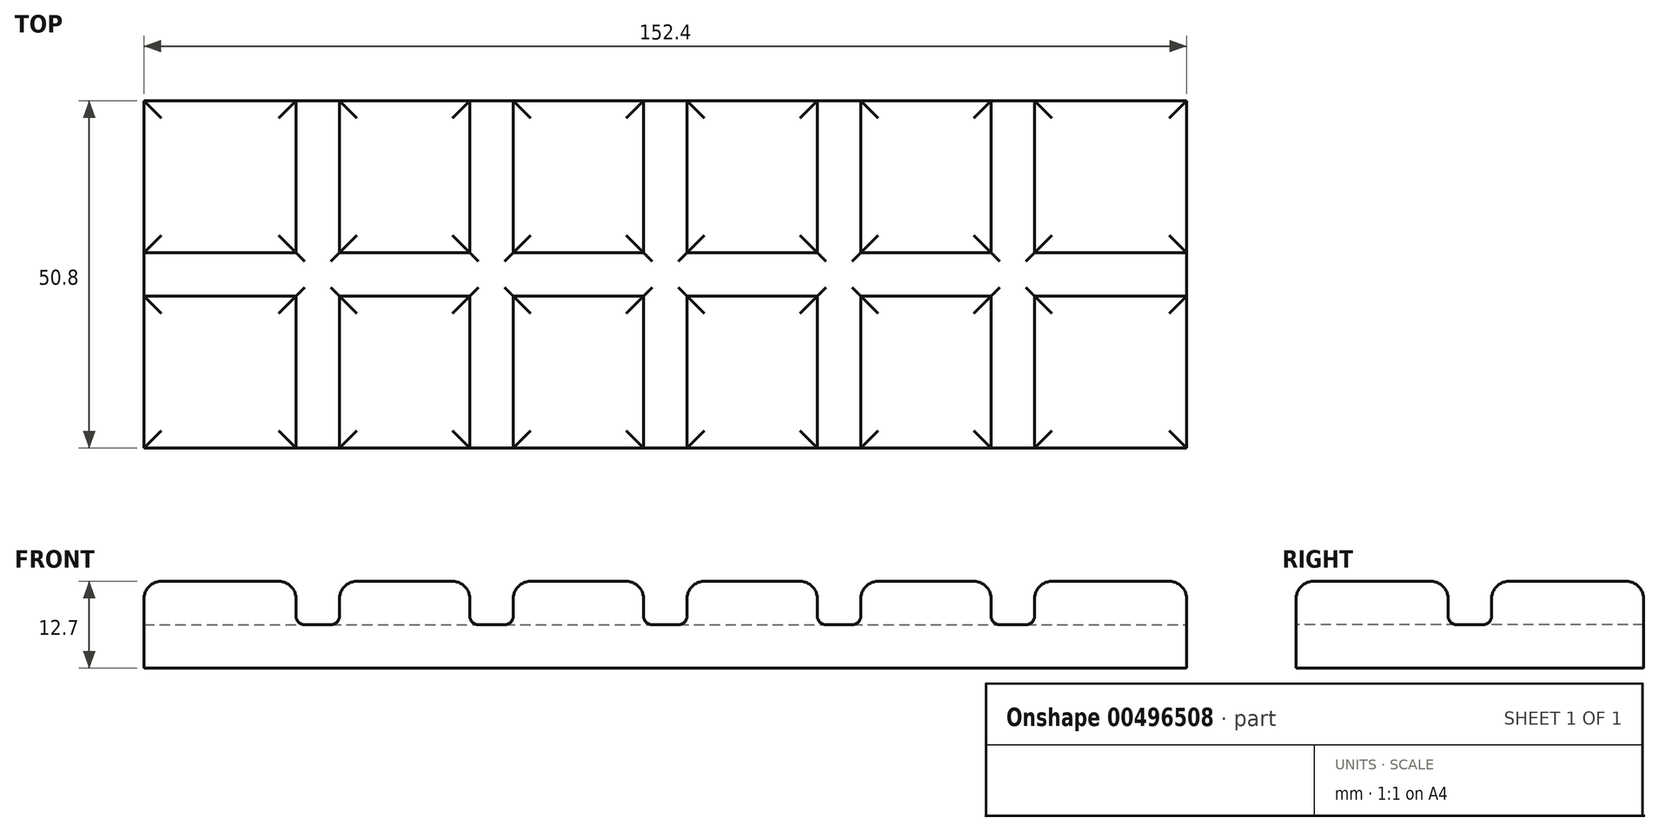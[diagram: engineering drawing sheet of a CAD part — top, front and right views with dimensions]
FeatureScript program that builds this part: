
annotation { "Feature Type Name" : "Feature", "Feature Type Description" : "" }
export const myFeature = defineFeature(function(context is Context, id is Id, definition is map)
    precondition{}
    {
        {
            var Q0;
            Q0=qCreatedBy(makeId("Top.planeOp"),FACE);
            var sketch = newSketch(context, id + "F0", { "sketchPlane" : qUnion([Q0])});
            skLineSegment(sketch, "E0.bottom", {"start": v(-76.2, 25.4) * mm, "end": v(76.2, 25.4) * mm});
            skLineSegment(sketch, "E0.top", {"start": v(-76.2, -25.4) * mm, "end": v(76.2, -25.4) * mm});
            skLineSegment(sketch, "E0.left", {"start": v(-76.2, 25.4) * mm, "end": v(-76.2, -25.4) * mm});
            skLineSegment(sketch, "E0.right", {"start": v(76.2, 25.4) * mm, "end": v(76.2, -25.4) * mm});
            skPoint(sketch, "E0.middle", {"position": v(0, 0) * mm});
            skSolve(sketch);
        }
        {
            var Q0;
            Q0 = qSketchRegion(id + "F0", true);
            extrude(context, id + "F1", {"entities" : qUnion([Q0]), "depth" : 12.7 * mm});
        }
        {
            var Q0;
            Q0=makeQuery(id+"F1.opExtrude","SWEPT_FACE",FACE,{"disambiguationData":[OSD([sQuery(id+"F0.wireOp",EDGE,"E0.right")])]});
            var sketch = newSketch(context, id + "F2", { "sketchPlane" : qUnion([Q0])});
            skLineSegment(sketch, "E1.bottom", {"start": v(3.18, 19.05) * mm, "end": v(-3.17, 19.05) * mm});
            skLineSegment(sketch, "E1.top", {"start": v(3.18, 6.35) * mm, "end": v(-3.17, 6.35) * mm});
            skLineSegment(sketch, "E1.left", {"start": v(3.18, 19.05) * mm, "end": v(3.18, 6.35) * mm});
            skLineSegment(sketch, "E1.right", {"start": v(-3.17, 19.05) * mm, "end": v(-3.17, 6.35) * mm});
            skPoint(sketch, "E1.middle", {"position": v(0, 12.7) * mm});
            skSolve(sketch);
        }
        {
            var Q0;
            Q0 = qSketchRegion(id + "F2", true);
            var Q1;
            Q1=makeQuery(id+"F1.opExtrude","SWEPT_FACE",FACE,{"disambiguationData":[OSD([sQuery(id+"F0.wireOp",EDGE,"E0.left")])]});
            extrude(context, id + "F3", {"entities" : qUnion([Q0]), "operationType" : NewBodyOperationType.REMOVE, "endBound" : BoundingType.THROUGH_ALL, "oppositeDirection" : true, "endBoundEntityFace" : qUnion([Q1]), "depth" : 25.4 * mm});
        }
        {
            var Q0;
            Q0=makeQuery(id+"F1.opExtrude","SWEPT_FACE",FACE,{"disambiguationData":[OSD([sQuery(id+"F0.wireOp",EDGE,"E0.top")])]});
            var sketch = newSketch(context, id + "F4", { "sketchPlane" : qUnion([Q0])});
            skLineSegment(sketch, "E2", {"start": v(-81.97, 6.35) * mm, "end": v(82.24, 6.35) * mm, "construction": true});
            skPoint(sketch, "E2.startSnap0", {"position": v(-76.2, 6.35) * mm});
            skLineSegment(sketch, "E3.bottom", {"start": v(3.18, 6.35) * mm, "end": v(-3.17, 6.35) * mm});
            skLineSegment(sketch, "E3.top", {"start": v(3.18, 19.05) * mm, "end": v(-3.17, 19.05) * mm});
            skLineSegment(sketch, "E3.left", {"start": v(3.18, 6.35) * mm, "end": v(3.18, 19.05) * mm});
            skLineSegment(sketch, "E3.right", {"start": v(-3.17, 6.35) * mm, "end": v(-3.17, 19.05) * mm});
            skPoint(sketch, "E3.middle", {"position": v(0, 12.7) * mm});
            skLineSegment(sketch, "E4.bottom", {"start": v(28.58, 6.35) * mm, "end": v(22.23, 6.35) * mm});
            skLineSegment(sketch, "E4.top", {"start": v(28.58, 19.05) * mm, "end": v(22.23, 19.05) * mm});
            skLineSegment(sketch, "E4.left", {"start": v(28.58, 6.35) * mm, "end": v(28.58, 19.05) * mm});
            skLineSegment(sketch, "E4.right", {"start": v(22.23, 6.35) * mm, "end": v(22.23, 19.05) * mm});
            skPoint(sketch, "E4.middle", {"position": v(25.4, 12.7) * mm});
            skLineSegment(sketch, "E5.bottom", {"start": v(53.98, 6.35) * mm, "end": v(47.63, 6.35) * mm});
            skLineSegment(sketch, "E5.top", {"start": v(53.98, 19.05) * mm, "end": v(47.63, 19.05) * mm});
            skLineSegment(sketch, "E5.left", {"start": v(53.98, 6.35) * mm, "end": v(53.98, 19.05) * mm});
            skLineSegment(sketch, "E5.right", {"start": v(47.63, 6.35) * mm, "end": v(47.63, 19.05) * mm});
            skPoint(sketch, "E5.middle", {"position": v(50.8, 12.7) * mm});
            skLineSegment(sketch, "E6.bottom", {"start": v(-22.23, 6.35) * mm, "end": v(-28.58, 6.35) * mm});
            skLineSegment(sketch, "E6.top", {"start": v(-22.23, 19.05) * mm, "end": v(-28.58, 19.05) * mm});
            skLineSegment(sketch, "E6.left", {"start": v(-22.23, 6.35) * mm, "end": v(-22.23, 19.05) * mm});
            skLineSegment(sketch, "E6.right", {"start": v(-28.58, 6.35) * mm, "end": v(-28.58, 19.05) * mm});
            skPoint(sketch, "E6.middle", {"position": v(-25.4, 12.7) * mm});
            skLineSegment(sketch, "E7.bottom", {"start": v(-47.63, 6.35) * mm, "end": v(-53.98, 6.35) * mm});
            skLineSegment(sketch, "E7.top", {"start": v(-47.63, 19.05) * mm, "end": v(-53.98, 19.05) * mm});
            skLineSegment(sketch, "E7.left", {"start": v(-47.63, 6.35) * mm, "end": v(-47.63, 19.05) * mm});
            skLineSegment(sketch, "E7.right", {"start": v(-53.98, 6.35) * mm, "end": v(-53.98, 19.05) * mm});
            skPoint(sketch, "E7.middle", {"position": v(-50.8, 12.7) * mm});
            skSolve(sketch);
        }
        {
            var Q0;
            Q0 = qSketchRegion(id + "F4", true);
            extrude(context, id + "F5", {"entities" : qUnion([Q0]), "operationType" : NewBodyOperationType.REMOVE, "endBound" : BoundingType.THROUGH_ALL, "oppositeDirection" : true, "depth" : 25.4 * mm});
        }
        {
            var Q0;
            {var subQ0=sQuery(id+"F0.wireOp",EDGE,"E0.top");var subQ1=makeQuery(id+"F1.opExtrude","SWEPT_FACE",FACE,{"disambiguationData":[OSD([subQ0])]});var subQ2=sQuery(id+"F0.wireOp",EDGE,"E0.left");var subQ3=makeQuery(id+"F1.opExtrude","SWEPT_FACE",FACE,{"disambiguationData":[OSD([subQ2])]});var subQ5=sQuery(id+"F0.wireOp",EDGE,"E0.right");Q0=makeQuery(id+"F5.boolean.opBoolean","SPLIT",FACE,{"disambiguationData":[TD([subQ3])],"derivedFrom":makeQuery(id+"F3.boolean.opBoolean","SPLIT",FACE,{"disambiguationData":[TD([subQ1])],"derivedFrom":makeQuery(id+"F1.opExtrude","CAP_FACE",FACE,{"disambiguationData":[OSD([sQuery(id+"F0.wireOp",EDGE,"E0.bottom"),subQ0,subQ2,subQ5])],"isStart":false})})});}
            var Q1;
            {var subQ0=sQuery(id+"F0.wireOp",EDGE,"E0.top");var subQ1=makeQuery(id+"F1.opExtrude","SWEPT_FACE",FACE,{"disambiguationData":[OSD([subQ0])]});var subQ3=sQuery(id+"F0.wireOp",EDGE,"E0.left");var subQ4=sQuery(id+"F0.wireOp",EDGE,"E0.right");Q1=makeQuery(id+"F5.boolean.opBoolean","SPLIT",FACE,{"disambiguationData":[TD([makeQuery(id+"F5.opExtrude","SWEPT_FACE",FACE,{"disambiguationData":[OSD([sQuery(id+"F4.wireOp",EDGE,"E6.right")])]})])],"derivedFrom":makeQuery(id+"F3.boolean.opBoolean","SPLIT",FACE,{"disambiguationData":[TD([subQ1])],"derivedFrom":makeQuery(id+"F1.opExtrude","CAP_FACE",FACE,{"disambiguationData":[OSD([sQuery(id+"F0.wireOp",EDGE,"E0.bottom"),subQ0,subQ3,subQ4])],"isStart":false})})});}
            var Q2;
            {var subQ0=sQuery(id+"F0.wireOp",EDGE,"E0.top");var subQ1=makeQuery(id+"F1.opExtrude","SWEPT_FACE",FACE,{"disambiguationData":[OSD([subQ0])]});var subQ3=sQuery(id+"F0.wireOp",EDGE,"E0.left");var subQ4=sQuery(id+"F0.wireOp",EDGE,"E0.right");Q2=makeQuery(id+"F5.boolean.opBoolean","SPLIT",FACE,{"disambiguationData":[TD([makeQuery(id+"F5.opExtrude","SWEPT_FACE",FACE,{"disambiguationData":[OSD([sQuery(id+"F4.wireOp",EDGE,"E3.right")])]})])],"derivedFrom":makeQuery(id+"F3.boolean.opBoolean","SPLIT",FACE,{"disambiguationData":[TD([subQ1])],"derivedFrom":makeQuery(id+"F1.opExtrude","CAP_FACE",FACE,{"disambiguationData":[OSD([sQuery(id+"F0.wireOp",EDGE,"E0.bottom"),subQ0,subQ3,subQ4])],"isStart":false})})});}
            var Q3;
            {var subQ0=sQuery(id+"F0.wireOp",EDGE,"E0.top");var subQ1=makeQuery(id+"F1.opExtrude","SWEPT_FACE",FACE,{"disambiguationData":[OSD([subQ0])]});var subQ3=sQuery(id+"F0.wireOp",EDGE,"E0.left");var subQ4=sQuery(id+"F0.wireOp",EDGE,"E0.right");Q3=makeQuery(id+"F5.boolean.opBoolean","SPLIT",FACE,{"disambiguationData":[TD([makeQuery(id+"F5.opExtrude","SWEPT_FACE",FACE,{"disambiguationData":[OSD([sQuery(id+"F4.wireOp",EDGE,"E3.left")])]})])],"derivedFrom":makeQuery(id+"F3.boolean.opBoolean","SPLIT",FACE,{"disambiguationData":[TD([subQ1])],"derivedFrom":makeQuery(id+"F1.opExtrude","CAP_FACE",FACE,{"disambiguationData":[OSD([sQuery(id+"F0.wireOp",EDGE,"E0.bottom"),subQ0,subQ3,subQ4])],"isStart":false})})});}
            var Q4;
            {var subQ0=sQuery(id+"F0.wireOp",EDGE,"E0.top");var subQ1=makeQuery(id+"F1.opExtrude","SWEPT_FACE",FACE,{"disambiguationData":[OSD([subQ0])]});var subQ3=sQuery(id+"F0.wireOp",EDGE,"E0.left");var subQ4=sQuery(id+"F0.wireOp",EDGE,"E0.right");Q4=makeQuery(id+"F5.boolean.opBoolean","SPLIT",FACE,{"disambiguationData":[TD([makeQuery(id+"F5.opExtrude","SWEPT_FACE",FACE,{"disambiguationData":[OSD([sQuery(id+"F4.wireOp",EDGE,"E4.left")])]})])],"derivedFrom":makeQuery(id+"F3.boolean.opBoolean","SPLIT",FACE,{"disambiguationData":[TD([subQ1])],"derivedFrom":makeQuery(id+"F1.opExtrude","CAP_FACE",FACE,{"disambiguationData":[OSD([sQuery(id+"F0.wireOp",EDGE,"E0.bottom"),subQ0,subQ3,subQ4])],"isStart":false})})});}
            var Q5;
            {var subQ0=sQuery(id+"F0.wireOp",EDGE,"E0.top");var subQ1=makeQuery(id+"F1.opExtrude","SWEPT_FACE",FACE,{"disambiguationData":[OSD([subQ0])]});var subQ2=sQuery(id+"F0.wireOp",EDGE,"E0.right");var subQ3=makeQuery(id+"F1.opExtrude","SWEPT_FACE",FACE,{"disambiguationData":[OSD([subQ2])]});var subQ5=sQuery(id+"F0.wireOp",EDGE,"E0.left");Q5=makeQuery(id+"F5.boolean.opBoolean","SPLIT",FACE,{"disambiguationData":[TD([subQ3])],"derivedFrom":makeQuery(id+"F3.boolean.opBoolean","SPLIT",FACE,{"disambiguationData":[TD([subQ1])],"derivedFrom":makeQuery(id+"F1.opExtrude","CAP_FACE",FACE,{"disambiguationData":[OSD([sQuery(id+"F0.wireOp",EDGE,"E0.bottom"),subQ0,subQ5,subQ2])],"isStart":false})})});}
            var Q6;
            {var subQ0=sQuery(id+"F0.wireOp",EDGE,"E0.bottom");var subQ1=makeQuery(id+"F1.opExtrude","SWEPT_FACE",FACE,{"disambiguationData":[OSD([subQ0])]});var subQ2=sQuery(id+"F0.wireOp",EDGE,"E0.right");var subQ3=makeQuery(id+"F1.opExtrude","SWEPT_FACE",FACE,{"disambiguationData":[OSD([subQ2])]});var subQ5=sQuery(id+"F0.wireOp",EDGE,"E0.left");Q6=makeQuery(id+"F5.boolean.opBoolean","SPLIT",FACE,{"disambiguationData":[TD([subQ3])],"derivedFrom":makeQuery(id+"F3.boolean.opBoolean","SPLIT",FACE,{"disambiguationData":[TD([subQ1])],"derivedFrom":makeQuery(id+"F1.opExtrude","CAP_FACE",FACE,{"disambiguationData":[OSD([subQ0,sQuery(id+"F0.wireOp",EDGE,"E0.top"),subQ5,subQ2])],"isStart":false})})});}
            var Q7;
            {var subQ0=sQuery(id+"F0.wireOp",EDGE,"E0.bottom");var subQ1=makeQuery(id+"F1.opExtrude","SWEPT_FACE",FACE,{"disambiguationData":[OSD([subQ0])]});var subQ3=sQuery(id+"F0.wireOp",EDGE,"E0.right");var subQ4=sQuery(id+"F0.wireOp",EDGE,"E0.left");Q7=makeQuery(id+"F5.boolean.opBoolean","SPLIT",FACE,{"disambiguationData":[TD([makeQuery(id+"F5.opExtrude","SWEPT_FACE",FACE,{"disambiguationData":[OSD([sQuery(id+"F4.wireOp",EDGE,"E4.left")])]})])],"derivedFrom":makeQuery(id+"F3.boolean.opBoolean","SPLIT",FACE,{"disambiguationData":[TD([subQ1])],"derivedFrom":makeQuery(id+"F1.opExtrude","CAP_FACE",FACE,{"disambiguationData":[OSD([subQ0,sQuery(id+"F0.wireOp",EDGE,"E0.top"),subQ4,subQ3])],"isStart":false})})});}
            var Q8;
            {var subQ0=sQuery(id+"F0.wireOp",EDGE,"E0.bottom");var subQ1=makeQuery(id+"F1.opExtrude","SWEPT_FACE",FACE,{"disambiguationData":[OSD([subQ0])]});var subQ3=sQuery(id+"F0.wireOp",EDGE,"E0.right");var subQ4=sQuery(id+"F0.wireOp",EDGE,"E0.left");Q8=makeQuery(id+"F5.boolean.opBoolean","SPLIT",FACE,{"disambiguationData":[TD([makeQuery(id+"F5.opExtrude","SWEPT_FACE",FACE,{"disambiguationData":[OSD([sQuery(id+"F4.wireOp",EDGE,"E3.left")])]})])],"derivedFrom":makeQuery(id+"F3.boolean.opBoolean","SPLIT",FACE,{"disambiguationData":[TD([subQ1])],"derivedFrom":makeQuery(id+"F1.opExtrude","CAP_FACE",FACE,{"disambiguationData":[OSD([subQ0,sQuery(id+"F0.wireOp",EDGE,"E0.top"),subQ4,subQ3])],"isStart":false})})});}
            var Q9;
            {var subQ0=sQuery(id+"F0.wireOp",EDGE,"E0.bottom");var subQ1=makeQuery(id+"F1.opExtrude","SWEPT_FACE",FACE,{"disambiguationData":[OSD([subQ0])]});var subQ3=sQuery(id+"F0.wireOp",EDGE,"E0.right");var subQ4=sQuery(id+"F0.wireOp",EDGE,"E0.left");Q9=makeQuery(id+"F5.boolean.opBoolean","SPLIT",FACE,{"disambiguationData":[TD([makeQuery(id+"F5.opExtrude","SWEPT_FACE",FACE,{"disambiguationData":[OSD([sQuery(id+"F4.wireOp",EDGE,"E6.right")])]})])],"derivedFrom":makeQuery(id+"F3.boolean.opBoolean","SPLIT",FACE,{"disambiguationData":[TD([subQ1])],"derivedFrom":makeQuery(id+"F1.opExtrude","CAP_FACE",FACE,{"disambiguationData":[OSD([subQ0,sQuery(id+"F0.wireOp",EDGE,"E0.top"),subQ4,subQ3])],"isStart":false})})});}
            var Q10;
            {var subQ0=sQuery(id+"F0.wireOp",EDGE,"E0.bottom");var subQ1=makeQuery(id+"F1.opExtrude","SWEPT_FACE",FACE,{"disambiguationData":[OSD([subQ0])]});var subQ3=sQuery(id+"F0.wireOp",EDGE,"E0.right");var subQ4=sQuery(id+"F0.wireOp",EDGE,"E0.left");Q10=makeQuery(id+"F5.boolean.opBoolean","SPLIT",FACE,{"disambiguationData":[TD([makeQuery(id+"F5.opExtrude","SWEPT_FACE",FACE,{"disambiguationData":[OSD([sQuery(id+"F4.wireOp",EDGE,"E3.right")])]})])],"derivedFrom":makeQuery(id+"F3.boolean.opBoolean","SPLIT",FACE,{"disambiguationData":[TD([subQ1])],"derivedFrom":makeQuery(id+"F1.opExtrude","CAP_FACE",FACE,{"disambiguationData":[OSD([subQ0,sQuery(id+"F0.wireOp",EDGE,"E0.top"),subQ4,subQ3])],"isStart":false})})});}
            var Q11;
            {var subQ0=sQuery(id+"F0.wireOp",EDGE,"E0.bottom");var subQ1=makeQuery(id+"F1.opExtrude","SWEPT_FACE",FACE,{"disambiguationData":[OSD([subQ0])]});var subQ3=sQuery(id+"F0.wireOp",EDGE,"E0.left");var subQ4=makeQuery(id+"F1.opExtrude","SWEPT_FACE",FACE,{"disambiguationData":[OSD([subQ3])]});var subQ5=sQuery(id+"F0.wireOp",EDGE,"E0.right");Q11=makeQuery(id+"F5.boolean.opBoolean","SPLIT",FACE,{"disambiguationData":[TD([subQ4])],"derivedFrom":makeQuery(id+"F3.boolean.opBoolean","SPLIT",FACE,{"disambiguationData":[TD([subQ1])],"derivedFrom":makeQuery(id+"F1.opExtrude","CAP_FACE",FACE,{"disambiguationData":[OSD([subQ0,sQuery(id+"F0.wireOp",EDGE,"E0.top"),subQ3,subQ5])],"isStart":false})})});}
            fillet(context, id + "F6", {"entities" : qUnion([Q0, Q1, Q2, Q3, Q4, Q5, Q6, Q7, Q8, Q9, Q10, Q11]), "radius" : 2.54 * mm, "tangentPropagation" : true, "allowEdgeOverflow" : false});
        }
        {
            var Q0;
            {var subQ0=sQuery(id+"F4.wireOp",EDGE,"E7.left");var subQ1=sQuery(id+"F4.wireOp",EDGE,"E7.bottom");Q0=makeQuery(id+"F5.boolean.opBoolean","COPY",EDGE,{"disambiguationData":[TD([makeQuery(id+"F1.opExtrude","SWEPT_FACE",FACE,{"disambiguationData":[OSD([sQuery(id+"F0.wireOp",EDGE,"E0.bottom")])]})])],"derivedFrom":makeQuery(id+"F5.opExtrude","SWEPT_EDGE",EDGE,{"disambiguationData":[OSD([subQ1,subQ0])]})});}
            var Q1;
            {var subQ0=sQuery(id+"F4.wireOp",EDGE,"E7.right");var subQ1=sQuery(id+"F4.wireOp",EDGE,"E7.bottom");Q1=makeQuery(id+"F5.boolean.opBoolean","COPY",EDGE,{"disambiguationData":[TD([makeQuery(id+"F1.opExtrude","SWEPT_FACE",FACE,{"disambiguationData":[OSD([sQuery(id+"F0.wireOp",EDGE,"E0.bottom")])]})])],"derivedFrom":makeQuery(id+"F5.opExtrude","SWEPT_EDGE",EDGE,{"disambiguationData":[OSD([subQ1,subQ0])]})});}
            var Q2;
            {var subQ0=sQuery(id+"F4.wireOp",EDGE,"E7.right");var subQ1=sQuery(id+"F4.wireOp",EDGE,"E7.bottom");Q2=makeQuery(id+"F5.boolean.opBoolean","COPY",EDGE,{"disambiguationData":[TD([makeQuery(id+"F1.opExtrude","SWEPT_FACE",FACE,{"disambiguationData":[OSD([sQuery(id+"F0.wireOp",EDGE,"E0.top")])]})])],"derivedFrom":makeQuery(id+"F5.opExtrude","SWEPT_EDGE",EDGE,{"disambiguationData":[OSD([subQ1,subQ0])]})});}
            var Q3;
            {var subQ0=sQuery(id+"F4.wireOp",EDGE,"E7.left");var subQ1=sQuery(id+"F4.wireOp",EDGE,"E7.bottom");Q3=makeQuery(id+"F5.boolean.opBoolean","COPY",EDGE,{"disambiguationData":[TD([makeQuery(id+"F1.opExtrude","SWEPT_FACE",FACE,{"disambiguationData":[OSD([sQuery(id+"F0.wireOp",EDGE,"E0.top")])]})])],"derivedFrom":makeQuery(id+"F5.opExtrude","SWEPT_EDGE",EDGE,{"disambiguationData":[OSD([subQ1,subQ0])]})});}
            var Q4;
            {var subQ0=sQuery(id+"F4.wireOp",EDGE,"E6.left");var subQ1=sQuery(id+"F4.wireOp",EDGE,"E6.bottom");Q4=makeQuery(id+"F5.boolean.opBoolean","COPY",EDGE,{"disambiguationData":[TD([makeQuery(id+"F1.opExtrude","SWEPT_FACE",FACE,{"disambiguationData":[OSD([sQuery(id+"F0.wireOp",EDGE,"E0.top")])]})])],"derivedFrom":makeQuery(id+"F5.opExtrude","SWEPT_EDGE",EDGE,{"disambiguationData":[OSD([subQ1,subQ0])]})});}
            var Q5;
            {var subQ0=sQuery(id+"F4.wireOp",EDGE,"E6.right");var subQ1=sQuery(id+"F4.wireOp",EDGE,"E6.bottom");Q5=makeQuery(id+"F5.boolean.opBoolean","COPY",EDGE,{"disambiguationData":[TD([makeQuery(id+"F1.opExtrude","SWEPT_FACE",FACE,{"disambiguationData":[OSD([sQuery(id+"F0.wireOp",EDGE,"E0.top")])]})])],"derivedFrom":makeQuery(id+"F5.opExtrude","SWEPT_EDGE",EDGE,{"disambiguationData":[OSD([subQ1,subQ0])]})});}
            var Q6;
            {var subQ0=sQuery(id+"F4.wireOp",EDGE,"E6.right");var subQ1=sQuery(id+"F4.wireOp",EDGE,"E6.bottom");Q6=makeQuery(id+"F5.boolean.opBoolean","COPY",EDGE,{"disambiguationData":[TD([makeQuery(id+"F1.opExtrude","SWEPT_FACE",FACE,{"disambiguationData":[OSD([sQuery(id+"F0.wireOp",EDGE,"E0.bottom")])]})])],"derivedFrom":makeQuery(id+"F5.opExtrude","SWEPT_EDGE",EDGE,{"disambiguationData":[OSD([subQ1,subQ0])]})});}
            var Q7;
            {var subQ0=sQuery(id+"F4.wireOp",EDGE,"E6.left");var subQ1=sQuery(id+"F4.wireOp",EDGE,"E6.bottom");Q7=makeQuery(id+"F5.boolean.opBoolean","COPY",EDGE,{"disambiguationData":[TD([makeQuery(id+"F1.opExtrude","SWEPT_FACE",FACE,{"disambiguationData":[OSD([sQuery(id+"F0.wireOp",EDGE,"E0.bottom")])]})])],"derivedFrom":makeQuery(id+"F5.opExtrude","SWEPT_EDGE",EDGE,{"disambiguationData":[OSD([subQ1,subQ0])]})});}
            var Q8;
            {var subQ0=sQuery(id+"F4.wireOp",EDGE,"E3.bottom");var subQ1=sQuery(id+"F4.wireOp",EDGE,"E3.left");Q8=makeQuery(id+"F5.boolean.opBoolean","COPY",EDGE,{"disambiguationData":[TD([makeQuery(id+"F1.opExtrude","SWEPT_FACE",FACE,{"disambiguationData":[OSD([sQuery(id+"F0.wireOp",EDGE,"E0.top")])]})])],"derivedFrom":makeQuery(id+"F5.opExtrude","SWEPT_EDGE",EDGE,{"disambiguationData":[OSD([subQ0,subQ1])]})});}
            var Q9;
            {var subQ0=sQuery(id+"F4.wireOp",EDGE,"E3.bottom");var subQ1=sQuery(id+"F4.wireOp",EDGE,"E3.left");Q9=makeQuery(id+"F5.boolean.opBoolean","COPY",EDGE,{"disambiguationData":[TD([makeQuery(id+"F1.opExtrude","SWEPT_FACE",FACE,{"disambiguationData":[OSD([sQuery(id+"F0.wireOp",EDGE,"E0.bottom")])]})])],"derivedFrom":makeQuery(id+"F5.opExtrude","SWEPT_EDGE",EDGE,{"disambiguationData":[OSD([subQ0,subQ1])]})});}
            var Q10;
            {var subQ0=sQuery(id+"F4.wireOp",EDGE,"E3.bottom");var subQ1=sQuery(id+"F4.wireOp",EDGE,"E3.right");Q10=makeQuery(id+"F5.boolean.opBoolean","COPY",EDGE,{"disambiguationData":[TD([makeQuery(id+"F1.opExtrude","SWEPT_FACE",FACE,{"disambiguationData":[OSD([sQuery(id+"F0.wireOp",EDGE,"E0.bottom")])]})])],"derivedFrom":makeQuery(id+"F5.opExtrude","SWEPT_EDGE",EDGE,{"disambiguationData":[OSD([subQ0,subQ1])]})});}
            var Q11;
            {var subQ0=sQuery(id+"F4.wireOp",EDGE,"E3.bottom");var subQ1=sQuery(id+"F4.wireOp",EDGE,"E3.right");Q11=makeQuery(id+"F5.boolean.opBoolean","COPY",EDGE,{"disambiguationData":[TD([makeQuery(id+"F1.opExtrude","SWEPT_FACE",FACE,{"disambiguationData":[OSD([sQuery(id+"F0.wireOp",EDGE,"E0.top")])]})])],"derivedFrom":makeQuery(id+"F5.opExtrude","SWEPT_EDGE",EDGE,{"disambiguationData":[OSD([subQ0,subQ1])]})});}
            var Q12;
            {var subQ0=sQuery(id+"F4.wireOp",EDGE,"E4.right");var subQ1=sQuery(id+"F4.wireOp",EDGE,"E4.bottom");Q12=makeQuery(id+"F5.boolean.opBoolean","COPY",EDGE,{"disambiguationData":[TD([makeQuery(id+"F1.opExtrude","SWEPT_FACE",FACE,{"disambiguationData":[OSD([sQuery(id+"F0.wireOp",EDGE,"E0.bottom")])]})])],"derivedFrom":makeQuery(id+"F5.opExtrude","SWEPT_EDGE",EDGE,{"disambiguationData":[OSD([subQ1,subQ0])]})});}
            var Q13;
            {var subQ0=sQuery(id+"F4.wireOp",EDGE,"E4.right");var subQ1=sQuery(id+"F4.wireOp",EDGE,"E4.bottom");Q13=makeQuery(id+"F5.boolean.opBoolean","COPY",EDGE,{"disambiguationData":[TD([makeQuery(id+"F1.opExtrude","SWEPT_FACE",FACE,{"disambiguationData":[OSD([sQuery(id+"F0.wireOp",EDGE,"E0.top")])]})])],"derivedFrom":makeQuery(id+"F5.opExtrude","SWEPT_EDGE",EDGE,{"disambiguationData":[OSD([subQ1,subQ0])]})});}
            var Q14;
            {var subQ0=sQuery(id+"F4.wireOp",EDGE,"E4.left");var subQ1=sQuery(id+"F4.wireOp",EDGE,"E4.bottom");Q14=makeQuery(id+"F5.boolean.opBoolean","COPY",EDGE,{"disambiguationData":[TD([makeQuery(id+"F1.opExtrude","SWEPT_FACE",FACE,{"disambiguationData":[OSD([sQuery(id+"F0.wireOp",EDGE,"E0.top")])]})])],"derivedFrom":makeQuery(id+"F5.opExtrude","SWEPT_EDGE",EDGE,{"disambiguationData":[OSD([subQ1,subQ0])]})});}
            var Q15;
            {var subQ0=sQuery(id+"F4.wireOp",EDGE,"E4.left");var subQ1=sQuery(id+"F4.wireOp",EDGE,"E4.bottom");Q15=makeQuery(id+"F5.boolean.opBoolean","COPY",EDGE,{"disambiguationData":[TD([makeQuery(id+"F1.opExtrude","SWEPT_FACE",FACE,{"disambiguationData":[OSD([sQuery(id+"F0.wireOp",EDGE,"E0.bottom")])]})])],"derivedFrom":makeQuery(id+"F5.opExtrude","SWEPT_EDGE",EDGE,{"disambiguationData":[OSD([subQ1,subQ0])]})});}
            var Q16;
            {var subQ0=sQuery(id+"F4.wireOp",EDGE,"E5.right");var subQ1=sQuery(id+"F4.wireOp",EDGE,"E5.bottom");Q16=makeQuery(id+"F5.boolean.opBoolean","COPY",EDGE,{"disambiguationData":[TD([makeQuery(id+"F1.opExtrude","SWEPT_FACE",FACE,{"disambiguationData":[OSD([sQuery(id+"F0.wireOp",EDGE,"E0.bottom")])]})])],"derivedFrom":makeQuery(id+"F5.opExtrude","SWEPT_EDGE",EDGE,{"disambiguationData":[OSD([subQ1,subQ0])]})});}
            var Q17;
            {var subQ0=sQuery(id+"F4.wireOp",EDGE,"E5.bottom");var subQ1=sQuery(id+"F4.wireOp",EDGE,"E5.right");Q17=makeQuery(id+"F5.boolean.opBoolean","COPY",EDGE,{"disambiguationData":[TD([makeQuery(id+"F1.opExtrude","SWEPT_FACE",FACE,{"disambiguationData":[OSD([sQuery(id+"F0.wireOp",EDGE,"E0.top")])]})])],"derivedFrom":makeQuery(id+"F5.opExtrude","SWEPT_EDGE",EDGE,{"disambiguationData":[OSD([subQ0,subQ1])]})});}
            var Q18;
            {var subQ0=sQuery(id+"F4.wireOp",EDGE,"E5.left");var subQ1=sQuery(id+"F4.wireOp",EDGE,"E5.bottom");Q18=makeQuery(id+"F5.boolean.opBoolean","COPY",EDGE,{"disambiguationData":[TD([makeQuery(id+"F1.opExtrude","SWEPT_FACE",FACE,{"disambiguationData":[OSD([sQuery(id+"F0.wireOp",EDGE,"E0.bottom")])]})])],"derivedFrom":makeQuery(id+"F5.opExtrude","SWEPT_EDGE",EDGE,{"disambiguationData":[OSD([subQ1,subQ0])]})});}
            var Q19;
            {var subQ0=sQuery(id+"F4.wireOp",EDGE,"E5.bottom");var subQ1=sQuery(id+"F4.wireOp",EDGE,"E5.left");Q19=makeQuery(id+"F5.boolean.opBoolean","COPY",EDGE,{"disambiguationData":[TD([makeQuery(id+"F1.opExtrude","SWEPT_FACE",FACE,{"disambiguationData":[OSD([sQuery(id+"F0.wireOp",EDGE,"E0.top")])]})])],"derivedFrom":makeQuery(id+"F5.opExtrude","SWEPT_EDGE",EDGE,{"disambiguationData":[OSD([subQ0,subQ1])]})});}
            var Q20;
            {var subQ0=sQuery(id+"F2.wireOp",EDGE,"E1.right");var subQ1=sQuery(id+"F2.wireOp",EDGE,"E1.top");Q20=makeQuery(id+"F5.boolean.opBoolean","SPLIT",EDGE,{"disambiguationData":[TD([makeQuery(id+"F1.opExtrude","SWEPT_FACE",FACE,{"disambiguationData":[OSD([sQuery(id+"F0.wireOp",EDGE,"E0.right")])]})])],"derivedFrom":makeQuery(id+"F3.boolean.opBoolean","COPY",EDGE,{"derivedFrom":makeQuery(id+"F3.opExtrude","SWEPT_EDGE",EDGE,{"disambiguationData":[OSD([subQ1,subQ0])]})})});}
            var Q21;
            {var subQ0=sQuery(id+"F2.wireOp",EDGE,"E1.right");var subQ1=sQuery(id+"F2.wireOp",EDGE,"E1.top");Q21=makeQuery(id+"F5.boolean.opBoolean","SPLIT",EDGE,{"disambiguationData":[TD([makeQuery(id+"F5.opExtrude","SWEPT_FACE",FACE,{"disambiguationData":[OSD([sQuery(id+"F4.wireOp",EDGE,"E4.left")])]})])],"derivedFrom":makeQuery(id+"F3.boolean.opBoolean","COPY",EDGE,{"derivedFrom":makeQuery(id+"F3.opExtrude","SWEPT_EDGE",EDGE,{"disambiguationData":[OSD([subQ1,subQ0])]})})});}
            var Q22;
            {var subQ0=sQuery(id+"F2.wireOp",EDGE,"E1.right");var subQ1=sQuery(id+"F2.wireOp",EDGE,"E1.top");Q22=makeQuery(id+"F5.boolean.opBoolean","SPLIT",EDGE,{"disambiguationData":[TD([makeQuery(id+"F5.opExtrude","SWEPT_FACE",FACE,{"disambiguationData":[OSD([sQuery(id+"F4.wireOp",EDGE,"E3.left")])]})])],"derivedFrom":makeQuery(id+"F3.boolean.opBoolean","COPY",EDGE,{"derivedFrom":makeQuery(id+"F3.opExtrude","SWEPT_EDGE",EDGE,{"disambiguationData":[OSD([subQ1,subQ0])]})})});}
            var Q23;
            {var subQ0=sQuery(id+"F2.wireOp",EDGE,"E1.right");var subQ1=sQuery(id+"F2.wireOp",EDGE,"E1.top");Q23=makeQuery(id+"F5.boolean.opBoolean","SPLIT",EDGE,{"disambiguationData":[TD([makeQuery(id+"F5.opExtrude","SWEPT_FACE",FACE,{"disambiguationData":[OSD([sQuery(id+"F4.wireOp",EDGE,"E3.right")])]})])],"derivedFrom":makeQuery(id+"F3.boolean.opBoolean","COPY",EDGE,{"derivedFrom":makeQuery(id+"F3.opExtrude","SWEPT_EDGE",EDGE,{"disambiguationData":[OSD([subQ1,subQ0])]})})});}
            var Q24;
            {var subQ0=sQuery(id+"F2.wireOp",EDGE,"E1.right");var subQ1=sQuery(id+"F2.wireOp",EDGE,"E1.top");Q24=makeQuery(id+"F5.boolean.opBoolean","SPLIT",EDGE,{"disambiguationData":[TD([makeQuery(id+"F5.opExtrude","SWEPT_FACE",FACE,{"disambiguationData":[OSD([sQuery(id+"F4.wireOp",EDGE,"E6.right")])]})])],"derivedFrom":makeQuery(id+"F3.boolean.opBoolean","COPY",EDGE,{"derivedFrom":makeQuery(id+"F3.opExtrude","SWEPT_EDGE",EDGE,{"disambiguationData":[OSD([subQ1,subQ0])]})})});}
            var Q25;
            {var subQ0=sQuery(id+"F2.wireOp",EDGE,"E1.right");var subQ1=sQuery(id+"F2.wireOp",EDGE,"E1.top");Q25=makeQuery(id+"F5.boolean.opBoolean","SPLIT",EDGE,{"disambiguationData":[TD([makeQuery(id+"F1.opExtrude","SWEPT_FACE",FACE,{"disambiguationData":[OSD([sQuery(id+"F0.wireOp",EDGE,"E0.left")])]})])],"derivedFrom":makeQuery(id+"F3.boolean.opBoolean","COPY",EDGE,{"derivedFrom":makeQuery(id+"F3.opExtrude","SWEPT_EDGE",EDGE,{"disambiguationData":[OSD([subQ1,subQ0])]})})});}
            var Q26;
            {var subQ0=sQuery(id+"F2.wireOp",EDGE,"E1.left");var subQ1=sQuery(id+"F2.wireOp",EDGE,"E1.top");Q26=makeQuery(id+"F5.boolean.opBoolean","SPLIT",EDGE,{"disambiguationData":[TD([makeQuery(id+"F1.opExtrude","SWEPT_FACE",FACE,{"disambiguationData":[OSD([sQuery(id+"F0.wireOp",EDGE,"E0.left")])]})])],"derivedFrom":makeQuery(id+"F3.boolean.opBoolean","COPY",EDGE,{"derivedFrom":makeQuery(id+"F3.opExtrude","SWEPT_EDGE",EDGE,{"disambiguationData":[OSD([subQ1,subQ0])]})})});}
            var Q27;
            {var subQ0=sQuery(id+"F2.wireOp",EDGE,"E1.left");var subQ1=sQuery(id+"F2.wireOp",EDGE,"E1.top");Q27=makeQuery(id+"F5.boolean.opBoolean","SPLIT",EDGE,{"disambiguationData":[TD([makeQuery(id+"F5.opExtrude","SWEPT_FACE",FACE,{"disambiguationData":[OSD([sQuery(id+"F4.wireOp",EDGE,"E3.right")])]})])],"derivedFrom":makeQuery(id+"F3.boolean.opBoolean","COPY",EDGE,{"derivedFrom":makeQuery(id+"F3.opExtrude","SWEPT_EDGE",EDGE,{"disambiguationData":[OSD([subQ1,subQ0])]})})});}
            var Q28;
            {var subQ0=sQuery(id+"F2.wireOp",EDGE,"E1.left");var subQ1=sQuery(id+"F2.wireOp",EDGE,"E1.top");Q28=makeQuery(id+"F5.boolean.opBoolean","SPLIT",EDGE,{"disambiguationData":[TD([makeQuery(id+"F5.opExtrude","SWEPT_FACE",FACE,{"disambiguationData":[OSD([sQuery(id+"F4.wireOp",EDGE,"E6.right")])]})])],"derivedFrom":makeQuery(id+"F3.boolean.opBoolean","COPY",EDGE,{"derivedFrom":makeQuery(id+"F3.opExtrude","SWEPT_EDGE",EDGE,{"disambiguationData":[OSD([subQ1,subQ0])]})})});}
            var Q29;
            {var subQ0=sQuery(id+"F2.wireOp",EDGE,"E1.left");var subQ1=sQuery(id+"F2.wireOp",EDGE,"E1.top");Q29=makeQuery(id+"F5.boolean.opBoolean","SPLIT",EDGE,{"disambiguationData":[TD([makeQuery(id+"F5.opExtrude","SWEPT_FACE",FACE,{"disambiguationData":[OSD([sQuery(id+"F4.wireOp",EDGE,"E3.left")])]})])],"derivedFrom":makeQuery(id+"F3.boolean.opBoolean","COPY",EDGE,{"derivedFrom":makeQuery(id+"F3.opExtrude","SWEPT_EDGE",EDGE,{"disambiguationData":[OSD([subQ1,subQ0])]})})});}
            var Q30;
            {var subQ0=sQuery(id+"F2.wireOp",EDGE,"E1.left");var subQ1=sQuery(id+"F2.wireOp",EDGE,"E1.top");Q30=makeQuery(id+"F5.boolean.opBoolean","SPLIT",EDGE,{"disambiguationData":[TD([makeQuery(id+"F5.opExtrude","SWEPT_FACE",FACE,{"disambiguationData":[OSD([sQuery(id+"F4.wireOp",EDGE,"E4.left")])]})])],"derivedFrom":makeQuery(id+"F3.boolean.opBoolean","COPY",EDGE,{"derivedFrom":makeQuery(id+"F3.opExtrude","SWEPT_EDGE",EDGE,{"disambiguationData":[OSD([subQ1,subQ0])]})})});}
            var Q31;
            {var subQ0=sQuery(id+"F2.wireOp",EDGE,"E1.left");var subQ1=sQuery(id+"F2.wireOp",EDGE,"E1.top");Q31=makeQuery(id+"F5.boolean.opBoolean","SPLIT",EDGE,{"disambiguationData":[TD([makeQuery(id+"F1.opExtrude","SWEPT_FACE",FACE,{"disambiguationData":[OSD([sQuery(id+"F0.wireOp",EDGE,"E0.right")])]})])],"derivedFrom":makeQuery(id+"F3.boolean.opBoolean","COPY",EDGE,{"derivedFrom":makeQuery(id+"F3.opExtrude","SWEPT_EDGE",EDGE,{"disambiguationData":[OSD([subQ1,subQ0])]})})});}
            fillet(context, id + "F7", {"entities" : qUnion([Q0, Q1, Q2, Q3, Q4, Q5, Q6, Q7, Q8, Q9, Q10, Q11, Q12, Q13, Q14, Q15, Q16, Q17, Q18, Q19, Q20, Q21, Q22, Q23, Q24, Q25, Q26, Q27, Q28, Q29, Q30, Q31]), "radius" : 1.27 * mm, "tangentPropagation" : true, "allowEdgeOverflow" : false});
        }
    });
